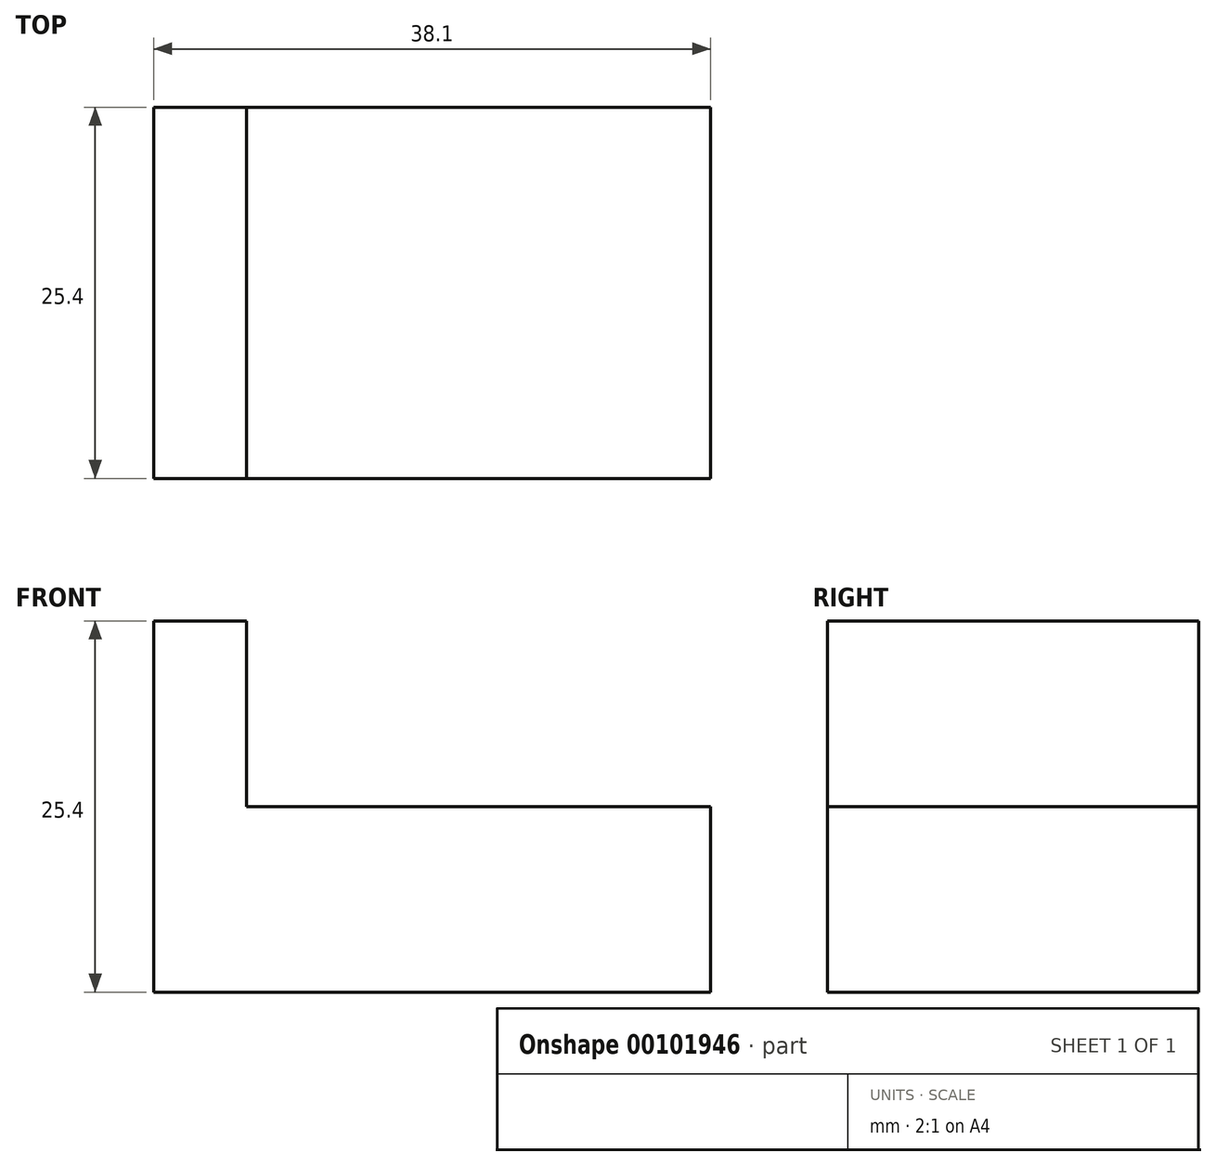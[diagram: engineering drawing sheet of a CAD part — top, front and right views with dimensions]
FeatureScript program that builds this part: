
annotation { "Feature Type Name" : "Feature", "Feature Type Description" : "" }
export const myFeature = defineFeature(function(context is Context, id is Id, definition is map)
    precondition{}
    {
        {
            var Q0;
            Q0=qCreatedBy(makeId("Front.planeOp"),FACE);
            var sketch = newSketch(context, id + "F0", { "sketchPlane" : qUnion([Q0])});
            skLineSegment(sketch, "E0", {"start": v(0, 0) * mm, "end": v(0, 25.4) * mm});
            skLineSegment(sketch, "E1", {"start": v(0, 25.4) * mm, "end": v(6.35, 25.4) * mm});
            skLineSegment(sketch, "E2", {"start": v(6.35, 25.4) * mm, "end": v(6.35, 12.7) * mm});
            skLineSegment(sketch, "E3", {"start": v(6.35, 12.7) * mm, "end": v(38.1, 12.7) * mm});
            skLineSegment(sketch, "E4", {"start": v(38.1, 12.7) * mm, "end": v(38.1, 0) * mm});
            skLineSegment(sketch, "E5", {"start": v(38.1, 0) * mm, "end": v(0, 0) * mm});
            skSolve(sketch);
        }
        {
            var Q0;
            Q0=makeQuery(id+"F0.imprint","IMPRINT",FACE,{"disambiguationData":[TD([[makeQuery(id+"F0.imprint","IMPRINT",EDGE,{"derivedFrom":sQuery(id+"F0.wireOp",EDGE,"E0")}),-1.0]])]});
            extrude(context, id + "F1", {"entities" : qUnion([Q0]), "oppositeDirection" : true, "depth" : 25.4 * mm});
        }
    });
